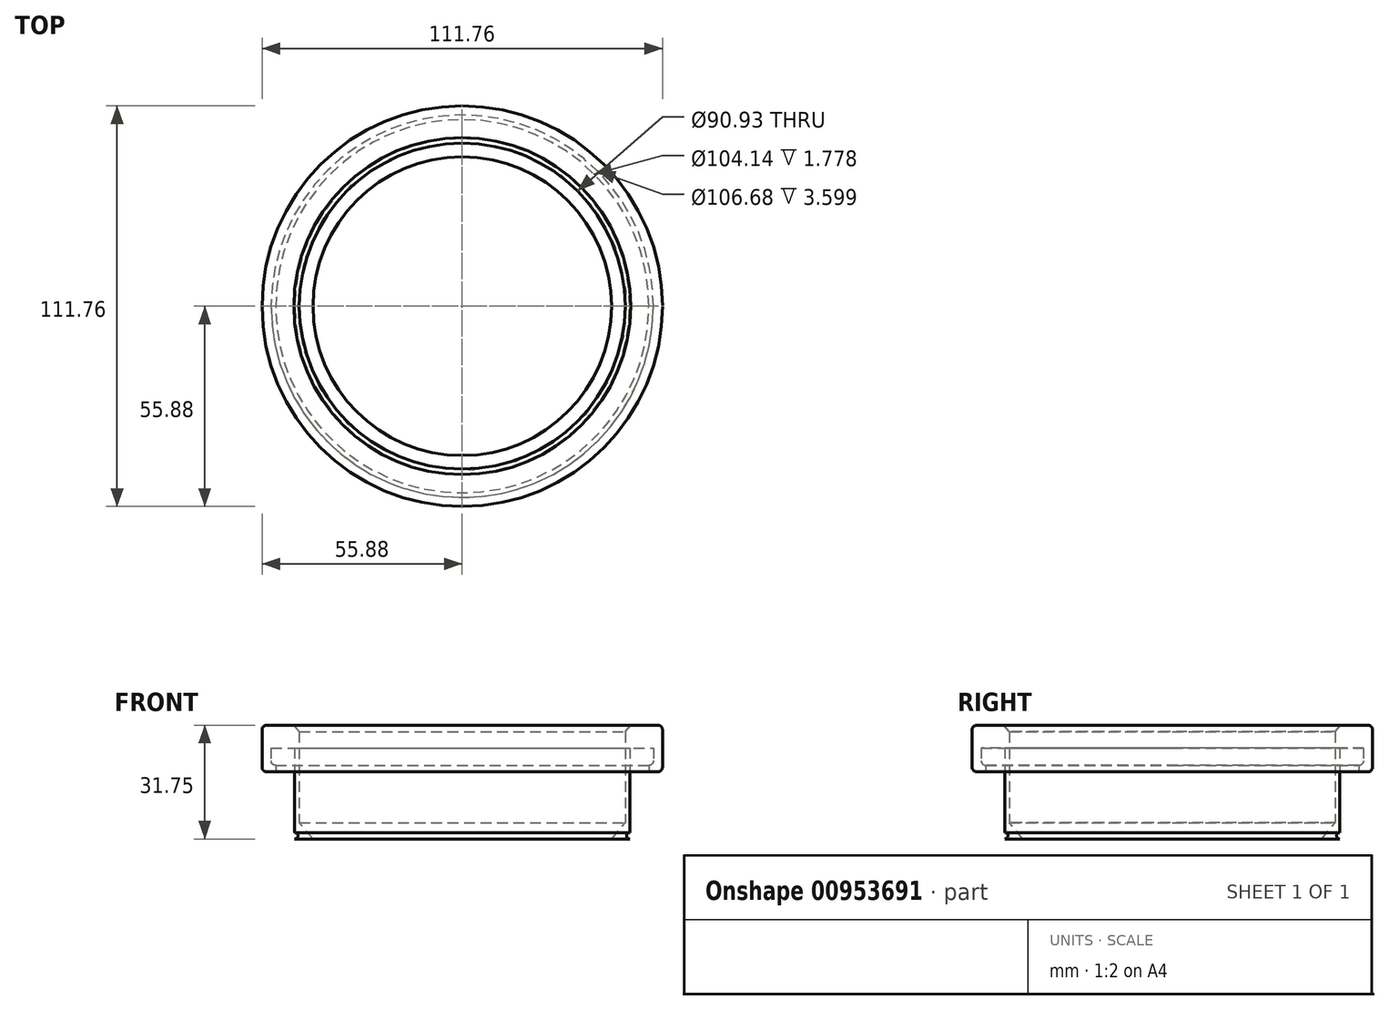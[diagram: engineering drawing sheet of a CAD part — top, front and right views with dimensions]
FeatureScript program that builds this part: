
annotation { "Feature Type Name" : "Feature", "Feature Type Description" : "" }
export const myFeature = defineFeature(function(context is Context, id is Id, definition is map)
    precondition{}
    {
        {
            var Q0;
            Q0=qCreatedBy(makeId("Front.planeOp"),FACE);
            var sketch = newSketch(context, id + "F0", { "sketchPlane" : qUnion([Q0])});
            skLineSegment(sketch, "E0", {"start": v(0, 0) * mm, "end": v(-16.51, 0) * mm});
            skLineSegment(sketch, "E1", {"start": v(-16.51, 0) * mm, "end": v(-41.66, 0) * mm});
            skLineSegment(sketch, "E2", {"start": v(0, 0) * mm, "end": v(0, 6.35) * mm});
            skLineSegment(sketch, "E3", {"start": v(0, 6.35) * mm, "end": v(-16.51, 6.35) * mm});
            skLineSegment(sketch, "E4", {"start": v(-16.51, 6.35) * mm, "end": v(-47, 6.35) * mm});
            skLineSegment(sketch, "E5", {"start": v(-47, 6.35) * mm, "end": v(-41.66, 0) * mm});
            skCircle(sketch, "E6", {"center": v(-49.01, -1.67) * mm, "radius": 1.59 * mm});
            skLineSegment(sketch, "E7", {"start": v(-53.34, -1.44) * mm, "end": v(-53.34, -4.87) * mm});
            skLineSegment(sketch, "E8", {"start": v(-53.34, -4.87) * mm, "end": v(-52.07, -4.87) * mm});
            skLineSegment(sketch, "E9", {"start": v(-52.07, -4.87) * mm, "end": v(-52.07, -6.65) * mm});
            skLineSegment(sketch, "E10", {"start": v(-52.07, -6.65) * mm, "end": v(-53.34, -6.65) * mm});
            skLineSegment(sketch, "E11", {"start": v(-53.34, -6.65) * mm, "end": v(-55.88, -6.65) * mm});
            skLineSegment(sketch, "E12", {"start": v(-55.88, -6.65) * mm, "end": v(-55.88, 6.35) * mm});
            skLineSegment(sketch, "E13", {"start": v(-55.88, 6.35) * mm, "end": v(-47, 6.35) * mm});
            skLineSegment(sketch, "E14", {"start": v(0, -15.02) * mm, "end": v(-47, -15.02) * mm});
            skLineSegment(sketch, "E15", {"start": v(-47, -15.02) * mm, "end": v(-47, 0) * mm});
            skLineSegment(sketch, "E16", {"start": v(-47, 6.35) * mm, "end": v(-47, -19.05) * mm});
            skLineSegment(sketch, "E17", {"start": v(-41.66, 0) * mm, "end": v(-41.66, -25.4) * mm});
            skLineSegment(sketch, "E18", {"start": v(-41.66, -25.4) * mm, "end": v(-46.99, -19.05) * mm});
            skLineSegment(sketch, "E19", {"start": v(0, 7.85) * mm, "end": v(-53.98, 7.85) * mm});
            skLineSegment(sketch, "E20", {"start": v(-41.66, -25.4) * mm, "end": v(-47, -25.4) * mm});
            skLineSegment(sketch, "E21", {"start": v(-47, -25.4) * mm, "end": v(-47, -19.05) * mm});
            skLineSegment(sketch, "E22", {"start": v(-47, 6.35) * mm, "end": v(-45.47, 6.35) * mm});
            skLineSegment(sketch, "E23", {"start": v(-45.47, 6.35) * mm, "end": v(-45.47, -25.4) * mm});
            skLineSegment(sketch, "E24", {"start": v(-53.34, -4.87) * mm, "end": v(-53.34, -6.65) * mm});
            skLineSegment(sketch, "E25", {"start": v(-47, 0) * mm, "end": v(-53.34, 0) * mm});
            skLineSegment(sketch, "E26", {"start": v(-53.34, 0) * mm, "end": v(-53.34, -1.44) * mm});
            skLineSegment(sketch, "E27", {"start": v(-47, 6.35) * mm, "end": v(-46.74, 6.35) * mm});
            skLineSegment(sketch, "E28", {"start": v(-46.74, 6.35) * mm, "end": v(-46.74, -25.4) * mm});
            skLineSegment(sketch, "E29", {"start": v(-52.07, -4.87) * mm, "end": v(-52.07, 0) * mm});
            skCircle(sketch, "E30", {"center": v(-46.74, -24.51) * mm, "radius": 0.89 * mm});
            skLineSegment(sketch, "E31", {"start": v(-46.74, -25.4) * mm, "end": v(-46.74, -24.51) * mm});
            skLineSegment(sketch, "E32", {"start": v(-47, 0) * mm, "end": v(-46.74, 0) * mm});
            skSolve(sketch);
        }
        {
            var Q0;
            {var subQ0=sQuery(id+"F0.wireOp",EDGE,"E31");Q0=makeQuery(id+"F0.imprint","IMPRINT",FACE,{"disambiguationData":[TD([[makeQuery(id+"F0.imprint","IMPRINT",EDGE,{"derivedFrom":subQ0}),-1.0]])]});}
            var Q1;
            {var subQ1=sQuery(id+"F0.wireOp",EDGE,"E18");var subQ5=sQuery(id+"F0.wireOp",EDGE,"E23");var subQ6=makeQuery(id+"F0.imprint","INTERSECT",VERTEX,{"derivedFrom":[subQ1,subQ5]});Q1=makeQuery(id+"F0.imprint","IMPRINT",FACE,{"disambiguationData":[TD([[makeQuery(id+"F0.imprint","IMPRINT",EDGE,{"disambiguationData":[TD([[subQ6,-1.0]])],"derivedFrom":subQ1}),1.0]])]});}
            var Q2;
            {var subQ0=sQuery(id+"F0.wireOp",EDGE,"E20");var subQ3=sQuery(id+"F0.wireOp",EDGE,"E23");var subQ5=makeQuery(id+"F0.imprint","INTERSECT",VERTEX,{"derivedFrom":[subQ0,subQ3]});Q2=makeQuery(id+"F0.imprint","IMPRINT",FACE,{"disambiguationData":[TD([[makeQuery(id+"F0.imprint","IMPRINT",EDGE,{"disambiguationData":[TD([[subQ5,1.0]])],"derivedFrom":subQ3}),1.0]])]});}
            var Q3;
            {var subQ0=sQuery(id+"F0.wireOp",EDGE,"E23");var subQ1=sQuery(id+"F0.wireOp",EDGE,"E14");var subQ2=makeQuery(id+"F0.imprint","INTERSECT",VERTEX,{"derivedFrom":[subQ1,subQ0]});Q3=makeQuery(id+"F0.imprint","IMPRINT",FACE,{"disambiguationData":[TD([[makeQuery(id+"F0.imprint","IMPRINT",EDGE,{"disambiguationData":[TD([[subQ2,-1.0]])],"derivedFrom":subQ1}),1.0]])]});}
            var Q4;
            {var subQ0=sQuery(id+"F0.wireOp",EDGE,"E28");var subQ2=sQuery(id+"F0.wireOp",EDGE,"E5");var subQ3=makeQuery(id+"F0.imprint","INTERSECT",VERTEX,{"derivedFrom":[subQ2,subQ0]});Q4=makeQuery(id+"F0.imprint","IMPRINT",FACE,{"disambiguationData":[TD([[makeQuery(id+"F0.imprint","IMPRINT",EDGE,{"disambiguationData":[TD([[subQ3,-1.0]])],"derivedFrom":subQ2}),-1.0]])]});}
            var Q5;
            {var subQ5=sQuery(id+"F0.wireOp",EDGE,"E32");Q5=makeQuery(id+"F0.imprint","IMPRINT",FACE,{"disambiguationData":[TD([[makeQuery(id+"F0.imprint","IMPRINT",EDGE,{"derivedFrom":subQ5}),1.0]])]});}
            var Q6;
            Q6=makeQuery(id+"F0.imprint","IMPRINT",FACE,{"disambiguationData":[TD([[makeQuery(id+"F0.imprint","IMPRINT",EDGE,{"derivedFrom":sQuery(id+"F0.wireOp",EDGE,"E7")}),-1.0]])]});
            var Q7;
            Q7=makeQuery(id+"F0.imprint","IMPRINT",FACE,{"disambiguationData":[TD([[makeQuery(id+"F0.imprint","IMPRINT",EDGE,{"derivedFrom":sQuery(id+"F0.wireOp",EDGE,"E8")}),-1.0]])]});
            var Q8;
            Q8=sQuery(id+"F0.wireOp",EDGE,"E2");
            revolve(context, id + "F1", {"surfaceOperationType" : NewSurfaceOperationType.NEW, "entities" : qUnion([Q0, Q1, Q2, Q3, Q4, Q5, Q6, Q7]), "axis" : qUnion([Q8]), "revolveType" : RevolveType.FULL});
        }
        {
            var Q0;
            Q0=makeQuery(id+"F1.opRevolve","SWEPT_EDGE",EDGE,{"disambiguationData":[OSD([sQuery(id+"F0.wireOp",EDGE,"E7"),sQuery(id+"F0.wireOp",EDGE,"E8")])]});
            var Q1;
            Q1=makeQuery(id+"F1.opRevolve","SWEPT_EDGE",EDGE,{"disambiguationData":[OSD([sQuery(id+"F0.wireOp",EDGE,"jxLSDtWP-QMUT-L3bA-y2mT-WSobOmcYYCXn"),sQuery(id+"F0.wireOp",EDGE,"E7")])]});
            var Q2;
            Q2=makeQuery(id+"F1.opRevolve","SWEPT_EDGE",EDGE,{"disambiguationData":[OSD([sQuery(id+"F0.wireOp",EDGE,"E12"),sQuery(id+"F0.wireOp",EDGE,"E13")])]});
            var Q3;
            Q3=makeQuery(id+"F1.opRevolve","SWEPT_EDGE",EDGE,{"disambiguationData":[OSD([sQuery(id+"F0.wireOp",EDGE,"E11"),sQuery(id+"F0.wireOp",EDGE,"E12")])]});
            fillet(context, id + "F2", {"entities" : qUnion([Q0, Q1, Q2, Q3]), "radius" : 1.27 * mm, "tangentPropagation" : true, "allowEdgeOverflow" : false});
        }
    });
